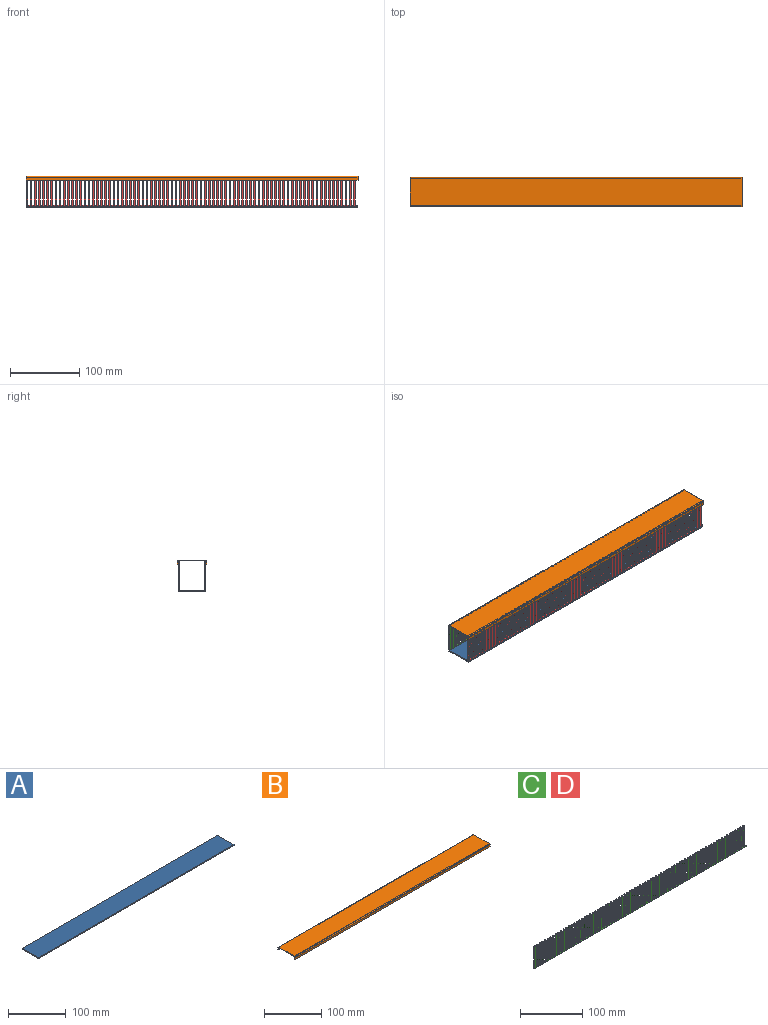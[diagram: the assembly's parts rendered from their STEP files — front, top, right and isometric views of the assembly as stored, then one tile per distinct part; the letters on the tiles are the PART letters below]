
ASSEMBLY  parts=4 mates=3
PART A: 6 faces, bbox 480x40x2 mm
  f0: plane 480.02x2mm, normal (0,1,0), area 960mm2, adj f1,f3,f4,f5
  f1: plane 40x2mm, normal (-1,0,0), area 80mm2, adj f0,f2,f4,f5
  f2: plane 480.02x2mm, normal (0,-1,0), area 960mm2, adj f1,f3,f4,f5
  f3: plane 40x2mm, normal (1,0,0), area 80mm2, adj f0,f2,f4,f5
  f4: plane 480.02x40mm, normal (0,0,1), area 19200.8mm2, adj f0,f1,f2,f3
  f5: plane 480.02x40mm, normal (0,0,-1), area 19200.8mm2, adj f0,f1,f2,f3
PART B: 12 faces, bbox 480.6x42x6 mm
  f0: plane 480.63x1mm, normal (0,0,-1), area 480.6mm2, adj f2,f3,f4,f7
  f1: plane 480.63x1mm, normal (0,0,-1), area 480.6mm2, adj f2,f4,f5,f8
  f2: plane 42x6mm, normal (-1,0,0), area 50.3mm2, adj f0,f1,f3,f5,f6,f7,f8,f9
  f3: plane 480.63x4mm, normal (0,-1,0), area 1922.5mm2, adj f0,f2,f4,f10
  f4: plane 42x6mm, normal (1,0,0), area 50.3mm2, adj f0,f1,f3,f5,f6,f7,f8,f9
  f5: plane 480.63x4mm, normal (0,1,0), area 1922.5mm2, adj f1,f2,f4,f11
  f6: plane 480.63x38mm, normal (0,0,1), area 18264.1mm2, adj f2,f4,f10,f11
  f7: plane 480.63x5mm, normal (0,1,0), area 2403.2mm2, adj f0,f2,f4,f9
  f8: plane 480.63x5mm, normal (0,-1,0), area 2403.2mm2, adj f1,f2,f4,f9
  f9: plane 480.63x40mm, normal (0,0,-1), area 19225.4mm2, adj f2,f4,f7,f8
  f10: cylinder r=2mm len=480.63mm, axis (-1,0,0), area 1510mm2, adj f2,f3,f4,f6
  f11: cylinder r=2mm len=480.63mm, axis (1,0,0), area 1510mm2, adj f2,f4,f5,f6
PART C: 324 faces, bbox 480x2x43.3 mm
  f0: plane 40x2mm, normal (-1,0,0), area 80mm2, adj f3,f5,f6,f8
  f1: plane 3.4x2mm, normal (0,0,1), area 6.8mm2, adj f2,f5,f6,f254
  f2: plane 40x2mm, normal (1,0,0), area 80mm2, adj f1,f3,f5,f6
  f3: cylinder r=1.3mm len=2.6mm, axis (0,1,0), area 8.2mm2, adj f0,f2,f5,f6
  f4: plane 480x2mm, normal (0,0,-1), area 960mm2, adj f5,f6,f214,f319
  f5: plane 480x43.3mm, normal (0,-1,0), area 9483.6mm2, adj f0,f1,f2,f3,f4,f7,f8,f9
  f6: plane 480x43.3mm, normal (0,1,0), area 9483.6mm2, adj f0,f1,f2,f3,f4,f7,f8,f9
  f7: plane 40x2mm, normal (-1,0,0), area 80mm2, adj f5,f6,f10,f12
  f8: plane 3.4x2mm, normal (0,0,1), area 6.8mm2, adj f0,f5,f6,f9
  f9: plane 40x2mm, normal (1,0,0), area 80mm2, adj f5,f6,f8,f10
  f10: cylinder r=1.3mm len=2.6mm, axis (0,1,0), area 8.2mm2, adj f5,f6,f7,f9
  f11: plane 40x2mm, normal (-1,0,0), area 80mm2, adj f5,f6,f14,f16
  f12: plane 3.4x2mm, normal (0,0,1), area 6.8mm2, adj f5,f6,f7,f13
  f13: plane 40x2mm, normal (1,0,0), area 80mm2, adj f5,f6,f12,f14
  f14: cylinder r=1.3mm len=2.6mm, axis (0,1,0), area 8.2mm2, adj f5,f6,f11,f13
  f15: plane 40x2mm, normal (-1,0,0), area 80mm2, adj f5,f6,f18,f20
  f16: plane 3.4x2mm, normal (0,0,1), area 6.8mm2, adj f5,f6,f11,f17
  f17: plane 40x2mm, normal (1,0,0), area 80mm2, adj f5,f6,f16,f18
  f18: cylinder r=1.3mm len=2.6mm, axis (0,1,0), area 8.2mm2, adj f5,f6,f15,f17
  f19: plane 40x2mm, normal (-1,0,0), area 80mm2, adj f5,f6,f22,f24
  f20: plane 3.4x2mm, normal (0,0,1), area 6.8mm2, adj f5,f6,f15,f21
  f21: plane 40x2mm, normal (1,0,0), area 80mm2, adj f5,f6,f20,f22
  f22: cylinder r=1.3mm len=2.6mm, axis (0,1,0), area 8.2mm2, adj f5,f6,f19,f21
  f23: plane 40x2mm, normal (-1,0,0), area 80mm2, adj f5,f6,f26,f28
  f24: plane 3.4x2mm, normal (0,0,1), area 6.8mm2, adj f5,f6,f19,f25
  f25: plane 40x2mm, normal (1,0,0), area 80mm2, adj f5,f6,f24,f26
  f26: cylinder r=1.3mm len=2.6mm, axis (0,1,0), area 8.2mm2, adj f5,f6,f23,f25
  f27: plane 40x2mm, normal (-1,0,0), area 80mm2, adj f5,f6,f30,f32
  f28: plane 3.4x2mm, normal (0,0,1), area 6.8mm2, adj f5,f6,f23,f29
  f29: plane 40x2mm, normal (1,0,0), area 80mm2, adj f5,f6,f28,f30
  f30: cylinder r=1.3mm len=2.6mm, axis (0,1,0), area 8.2mm2, adj f5,f6,f27,f29
  f31: plane 40x2mm, normal (-1,0,0), area 80mm2, adj f5,f6,f34,f36
  f32: plane 3.4x2mm, normal (0,0,1), area 6.8mm2, adj f5,f6,f27,f33
  f33: plane 40x2mm, normal (1,0,0), area 80mm2, adj f5,f6,f32,f34
  f34: cylinder r=1.3mm len=2.6mm, axis (0,1,0), area 8.2mm2, adj f5,f6,f31,f33
  f35: plane 40x2mm, normal (-1,0,0), area 80mm2, adj f5,f6,f38,f40
  f36: plane 3.4x2mm, normal (0,0,1), area 6.8mm2, adj f5,f6,f31,f37
  f37: plane 40x2mm, normal (1,0,0), area 80mm2, adj f5,f6,f36,f38
  f38: cylinder r=1.3mm len=2.6mm, axis (0,1,0), area 8.2mm2, adj f5,f6,f35,f37
  f39: plane 40x2mm, normal (-1,0,0), area 80mm2, adj f5,f6,f42,f44
  f40: plane 3.4x2mm, normal (0,0,1), area 6.8mm2, adj f5,f6,f35,f41
  f41: plane 40x2mm, normal (1,0,0), area 80mm2, adj f5,f6,f40,f42
  f42: cylinder r=1.3mm len=2.6mm, axis (0,1,0), area 8.2mm2, adj f5,f6,f39,f41
  f43: plane 40x2mm, normal (-1,0,0), area 80mm2, adj f5,f6,f46,f48
  f44: plane 3.4x2mm, normal (0,0,1), area 6.8mm2, adj f5,f6,f39,f45
  f45: plane 40x2mm, normal (1,0,0), area 80mm2, adj f5,f6,f44,f46
  f46: cylinder r=1.3mm len=2.6mm, axis (0,1,0), area 8.2mm2, adj f5,f6,f43,f45
  f47: plane 40x2mm, normal (-1,0,0), area 80mm2, adj f5,f6,f50,f52
  f48: plane 3.4x2mm, normal (0,0,1), area 6.8mm2, adj f5,f6,f43,f49
  f49: plane 40x2mm, normal (1,0,0), area 80mm2, adj f5,f6,f48,f50
  f50: cylinder r=1.3mm len=2.6mm, axis (0,1,0), area 8.2mm2, adj f5,f6,f47,f49
  f51: plane 40x2mm, normal (-1,0,0), area 80mm2, adj f5,f6,f54,f56
  f52: plane 3.4x2mm, normal (0,0,1), area 6.8mm2, adj f5,f6,f47,f53
  f53: plane 40x2mm, normal (1,0,0), area 80mm2, adj f5,f6,f52,f54
  f54: cylinder r=1.3mm len=2.6mm, axis (0,1,0), area 8.2mm2, adj f5,f6,f51,f53
  f55: plane 40x2mm, normal (-1,0,0), area 80mm2, adj f5,f6,f58,f60
  f56: plane 3.4x2mm, normal (0,0,1), area 6.8mm2, adj f5,f6,f51,f57
  f57: plane 40x2mm, normal (1,0,0), area 80mm2, adj f5,f6,f56,f58
  f58: cylinder r=1.3mm len=2.6mm, axis (0,1,0), area 8.2mm2, adj f5,f6,f55,f57
  f59: plane 40x2mm, normal (-1,0,0), area 80mm2, adj f5,f6,f62,f64
  f60: plane 3.4x2mm, normal (0,0,1), area 6.8mm2, adj f5,f6,f55,f61
  f61: plane 40x2mm, normal (1,0,0), area 80mm2, adj f5,f6,f60,f62
  f62: cylinder r=1.3mm len=2.6mm, axis (0,1,0), area 8.2mm2, adj f5,f6,f59,f61
  f63: plane 40x2mm, normal (-1,0,0), area 80mm2, adj f5,f6,f66,f68
  f64: plane 3.4x2mm, normal (0,0,1), area 6.8mm2, adj f5,f6,f59,f65
  f65: plane 40x2mm, normal (1,0,0), area 80mm2, adj f5,f6,f64,f66
  f66: cylinder r=1.3mm len=2.6mm, axis (0,1,0), area 8.2mm2, adj f5,f6,f63,f65
  f67: plane 40x2mm, normal (-1,0,0), area 80mm2, adj f5,f6,f70,f72
  f68: plane 3.4x2mm, normal (0,0,1), area 6.8mm2, adj f5,f6,f63,f69
  f69: plane 40x2mm, normal (1,0,0), area 80mm2, adj f5,f6,f68,f70
  f70: cylinder r=1.3mm len=2.6mm, axis (0,1,0), area 8.2mm2, adj f5,f6,f67,f69
  f71: plane 40x2mm, normal (-1,0,0), area 80mm2, adj f5,f6,f74,f76
  f72: plane 3.4x2mm, normal (0,0,1), area 6.8mm2, adj f5,f6,f67,f73
  f73: plane 40x2mm, normal (1,0,0), area 80mm2, adj f5,f6,f72,f74
  f74: cylinder r=1.3mm len=2.6mm, axis (0,1,0), area 8.2mm2, adj f5,f6,f71,f73
  f75: plane 40x2mm, normal (-1,0,0), area 80mm2, adj f5,f6,f78,f80
  f76: plane 3.4x2mm, normal (0,0,1), area 6.8mm2, adj f5,f6,f71,f77
  f77: plane 40x2mm, normal (1,0,0), area 80mm2, adj f5,f6,f76,f78
  f78: cylinder r=1.3mm len=2.6mm, axis (0,1,0), area 8.2mm2, adj f5,f6,f75,f77
  f79: plane 40x2mm, normal (-1,0,0), area 80mm2, adj f5,f6,f82,f84
  f80: plane 3.4x2mm, normal (0,0,1), area 6.8mm2, adj f5,f6,f75,f81
  f81: plane 40x2mm, normal (1,0,0), area 80mm2, adj f5,f6,f80,f82
  f82: cylinder r=1.3mm len=2.6mm, axis (0,1,0), area 8.2mm2, adj f5,f6,f79,f81
  f83: plane 40x2mm, normal (-1,0,0), area 80mm2, adj f5,f6,f86,f88
  f84: plane 3.4x2mm, normal (0,0,1), area 6.8mm2, adj f5,f6,f79,f85
  f85: plane 40x2mm, normal (1,0,0), area 80mm2, adj f5,f6,f84,f86
  f86: cylinder r=1.3mm len=2.6mm, axis (0,1,0), area 8.2mm2, adj f5,f6,f83,f85
  f87: plane 40x2mm, normal (-1,0,0), area 80mm2, adj f5,f6,f90,f92
  f88: plane 3.4x2mm, normal (0,0,1), area 6.8mm2, adj f5,f6,f83,f89
  f89: plane 40x2mm, normal (1,0,0), area 80mm2, adj f5,f6,f88,f90
  f90: cylinder r=1.3mm len=2.6mm, axis (0,1,0), area 8.2mm2, adj f5,f6,f87,f89
  f91: plane 40x2mm, normal (-1,0,0), area 80mm2, adj f5,f6,f94,f96
  f92: plane 3.4x2mm, normal (0,0,1), area 6.8mm2, adj f5,f6,f87,f93
  f93: plane 40x2mm, normal (1,0,0), area 80mm2, adj f5,f6,f92,f94
  f94: cylinder r=1.3mm len=2.6mm, axis (0,1,0), area 8.2mm2, adj f5,f6,f91,f93
  f95: plane 40x2mm, normal (-1,0,0), area 80mm2, adj f5,f6,f98,f100
  f96: plane 3.4x2mm, normal (0,0,1), area 6.8mm2, adj f5,f6,f91,f97
  f97: plane 40x2mm, normal (1,0,0), area 80mm2, adj f5,f6,f96,f98
  f98: cylinder r=1.3mm len=2.6mm, axis (0,1,0), area 8.2mm2, adj f5,f6,f95,f97
  f99: plane 40x2mm, normal (-1,0,0), area 80mm2, adj f5,f6,f102,f104
  f100: plane 3.4x2mm, normal (0,0,1), area 6.8mm2, adj f5,f6,f95,f101
  f101: plane 40x2mm, normal (1,0,0), area 80mm2, adj f5,f6,f100,f102
  f102: cylinder r=1.3mm len=2.6mm, axis (0,1,0), area 8.2mm2, adj f5,f6,f99,f101
  f103: plane 40x2mm, normal (-1,0,0), area 80mm2, adj f5,f6,f106,f108
  f104: plane 3.4x2mm, normal (0,0,1), area 6.8mm2, adj f5,f6,f99,f105
  f105: plane 40x2mm, normal (1,0,0), area 80mm2, adj f5,f6,f104,f106
  f106: cylinder r=1.3mm len=2.6mm, axis (0,1,0), area 8.2mm2, adj f5,f6,f103,f105
  f107: plane 40x2mm, normal (-1,0,0), area 80mm2, adj f5,f6,f110,f112
  f108: plane 3.4x2mm, normal (0,0,1), area 6.8mm2, adj f5,f6,f103,f109
  f109: plane 40x2mm, normal (1,0,0), area 80mm2, adj f5,f6,f108,f110
  f110: cylinder r=1.3mm len=2.6mm, axis (0,1,0), area 8.2mm2, adj f5,f6,f107,f109
  f111: plane 40x2mm, normal (-1,0,0), area 80mm2, adj f5,f6,f114,f116
  f112: plane 3.4x2mm, normal (0,0,1), area 6.8mm2, adj f5,f6,f107,f113
  f113: plane 40x2mm, normal (1,0,0), area 80mm2, adj f5,f6,f112,f114
  f114: cylinder r=1.3mm len=2.6mm, axis (0,1,0), area 8.2mm2, adj f5,f6,f111,f113
  f115: plane 40x2mm, normal (-1,0,0), area 80mm2, adj f5,f6,f118,f120
  f116: plane 3.4x2mm, normal (0,0,1), area 6.8mm2, adj f5,f6,f111,f117
  f117: plane 40x2mm, normal (1,0,0), area 80mm2, adj f5,f6,f116,f118
  f118: cylinder r=1.3mm len=2.6mm, axis (0,1,0), area 8.2mm2, adj f5,f6,f115,f117
  f119: plane 40x2mm, normal (-1,0,0), area 80mm2, adj f5,f6,f122,f124
  f120: plane 3.4x2mm, normal (0,0,1), area 6.8mm2, adj f5,f6,f115,f121
  f121: plane 40x2mm, normal (1,0,0), area 80mm2, adj f5,f6,f120,f122
  f122: cylinder r=1.3mm len=2.6mm, axis (0,1,0), area 8.2mm2, adj f5,f6,f119,f121
  f123: plane 40x2mm, normal (-1,0,0), area 80mm2, adj f5,f6,f126,f128
  f124: plane 3.4x2mm, normal (0,0,1), area 6.8mm2, adj f5,f6,f119,f125
  f125: plane 40x2mm, normal (1,0,0), area 80mm2, adj f5,f6,f124,f126
  f126: cylinder r=1.3mm len=2.6mm, axis (0,1,0), area 8.2mm2, adj f5,f6,f123,f125
  f127: plane 40x2mm, normal (-1,0,0), area 80mm2, adj f5,f6,f130,f132
  f128: plane 3.4x2mm, normal (0,0,1), area 6.8mm2, adj f5,f6,f123,f129
  f129: plane 40x2mm, normal (1,0,0), area 80mm2, adj f5,f6,f128,f130
  f130: cylinder r=1.3mm len=2.6mm, axis (0,1,0), area 8.2mm2, adj f5,f6,f127,f129
  f131: plane 40x2mm, normal (-1,0,0), area 80mm2, adj f5,f6,f134,f136
  f132: plane 3.4x2mm, normal (0,0,1), area 6.8mm2, adj f5,f6,f127,f133
  f133: plane 40x2mm, normal (1,0,0), area 80mm2, adj f5,f6,f132,f134
  f134: cylinder r=1.3mm len=2.6mm, axis (0,1,0), area 8.2mm2, adj f5,f6,f131,f133
  f135: plane 40x2mm, normal (-1,0,0), area 80mm2, adj f5,f6,f138,f140
  f136: plane 3.4x2mm, normal (0,0,1), area 6.8mm2, adj f5,f6,f131,f137
  f137: plane 40x2mm, normal (1,0,0), area 80mm2, adj f5,f6,f136,f138
  f138: cylinder r=1.3mm len=2.6mm, axis (0,1,0), area 8.2mm2, adj f5,f6,f135,f137
  f139: plane 40x2mm, normal (-1,0,0), area 80mm2, adj f5,f6,f142,f144
  f140: plane 3.4x2mm, normal (0,0,1), area 6.8mm2, adj f5,f6,f135,f141
  f141: plane 40x2mm, normal (1,0,0), area 80mm2, adj f5,f6,f140,f142
  f142: cylinder r=1.3mm len=2.6mm, axis (0,1,0), area 8.2mm2, adj f5,f6,f139,f141
  f143: plane 40x2mm, normal (-1,0,0), area 80mm2, adj f5,f6,f146,f148
  f144: plane 3.4x2mm, normal (0,0,1), area 6.8mm2, adj f5,f6,f139,f145
  f145: plane 40x2mm, normal (1,0,0), area 80mm2, adj f5,f6,f144,f146
  f146: cylinder r=1.3mm len=2.6mm, axis (0,1,0), area 8.2mm2, adj f5,f6,f143,f145
  f147: plane 40x2mm, normal (-1,0,0), area 80mm2, adj f5,f6,f150,f152
  f148: plane 3.4x2mm, normal (0,0,1), area 6.8mm2, adj f5,f6,f143,f149
  f149: plane 40x2mm, normal (1,0,0), area 80mm2, adj f5,f6,f148,f150
  f150: cylinder r=1.3mm len=2.6mm, axis (0,1,0), area 8.2mm2, adj f5,f6,f147,f149
  f151: plane 40x2mm, normal (-1,0,0), area 80mm2, adj f5,f6,f154,f156
  f152: plane 3.4x2mm, normal (0,0,1), area 6.8mm2, adj f5,f6,f147,f153
  f153: plane 40x2mm, normal (1,0,0), area 80mm2, adj f5,f6,f152,f154
  f154: cylinder r=1.3mm len=2.6mm, axis (0,1,0), area 8.2mm2, adj f5,f6,f151,f153
  f155: plane 40x2mm, normal (-1,0,0), area 80mm2, adj f5,f6,f158,f160
  f156: plane 3.4x2mm, normal (0,0,1), area 6.8mm2, adj f5,f6,f151,f157
  f157: plane 40x2mm, normal (1,0,0), area 80mm2, adj f5,f6,f156,f158
  f158: cylinder r=1.3mm len=2.6mm, axis (0,1,0), area 8.2mm2, adj f5,f6,f155,f157
  f159: plane 40x2mm, normal (-1,0,0), area 80mm2, adj f5,f6,f162,f164
  f160: plane 3.4x2mm, normal (0,0,1), area 6.8mm2, adj f5,f6,f155,f161
  f161: plane 40x2mm, normal (1,0,0), area 80mm2, adj f5,f6,f160,f162
  f162: cylinder r=1.3mm len=2.6mm, axis (0,1,0), area 8.2mm2, adj f5,f6,f159,f161
  f163: plane 40x2mm, normal (-1,0,0), area 80mm2, adj f5,f6,f166,f168
  f164: plane 3.4x2mm, normal (0,0,1), area 6.8mm2, adj f5,f6,f159,f165
  f165: plane 40x2mm, normal (1,0,0), area 80mm2, adj f5,f6,f164,f166
  f166: cylinder r=1.3mm len=2.6mm, axis (0,1,0), area 8.2mm2, adj f5,f6,f163,f165
  f167: plane 40x2mm, normal (-1,0,0), area 80mm2, adj f5,f6,f170,f172
  f168: plane 3.4x2mm, normal (0,0,1), area 6.8mm2, adj f5,f6,f163,f169
  f169: plane 40x2mm, normal (1,0,0), area 80mm2, adj f5,f6,f168,f170
  f170: cylinder r=1.3mm len=2.6mm, axis (0,1,0), area 8.2mm2, adj f5,f6,f167,f169
  f171: plane 40x2mm, normal (-1,0,0), area 80mm2, adj f5,f6,f174,f176
  f172: plane 3.4x2mm, normal (0,0,1), area 6.8mm2, adj f5,f6,f167,f173
  f173: plane 40x2mm, normal (1,0,0), area 80mm2, adj f5,f6,f172,f174
  f174: cylinder r=1.3mm len=2.6mm, axis (0,1,0), area 8.2mm2, adj f5,f6,f171,f173
  f175: plane 40x2mm, normal (-1,0,0), area 80mm2, adj f5,f6,f178,f180
  f176: plane 3.4x2mm, normal (0,0,1), area 6.8mm2, adj f5,f6,f171,f177
  f177: plane 40x2mm, normal (1,0,0), area 80mm2, adj f5,f6,f176,f178
  f178: cylinder r=1.3mm len=2.6mm, axis (0,1,0), area 8.2mm2, adj f5,f6,f175,f177
  f179: plane 40x2mm, normal (-1,0,0), area 80mm2, adj f5,f6,f182,f184
  f180: plane 3.4x2mm, normal (0,0,1), area 6.8mm2, adj f5,f6,f175,f181
  f181: plane 40x2mm, normal (1,0,0), area 80mm2, adj f5,f6,f180,f182
  f182: cylinder r=1.3mm len=2.6mm, axis (0,1,0), area 8.2mm2, adj f5,f6,f179,f181
  f183: plane 40x2mm, normal (-1,0,0), area 80mm2, adj f5,f6,f186,f188
  f184: plane 3.4x2mm, normal (0,0,1), area 6.8mm2, adj f5,f6,f179,f185
  f185: plane 40x2mm, normal (1,0,0), area 80mm2, adj f5,f6,f184,f186
  f186: cylinder r=1.3mm len=2.6mm, axis (0,1,0), area 8.2mm2, adj f5,f6,f183,f185
  f187: plane 40x2mm, normal (-1,0,0), area 80mm2, adj f5,f6,f190,f192
  f188: plane 3.4x2mm, normal (0,0,1), area 6.8mm2, adj f5,f6,f183,f189
  f189: plane 40x2mm, normal (1,0,0), area 80mm2, adj f5,f6,f188,f190
  f190: cylinder r=1.3mm len=2.6mm, axis (0,1,0), area 8.2mm2, adj f5,f6,f187,f189
  f191: plane 40x2mm, normal (-1,0,0), area 80mm2, adj f5,f6,f194,f196
  f192: plane 3.4x2mm, normal (0,0,1), area 6.8mm2, adj f5,f6,f187,f193
  f193: plane 40x2mm, normal (1,0,0), area 80mm2, adj f5,f6,f192,f194
  f194: cylinder r=1.3mm len=2.6mm, axis (0,1,0), area 8.2mm2, adj f5,f6,f191,f193
  f195: plane 40x2mm, normal (-1,0,0), area 80mm2, adj f5,f6,f198,f200
  f196: plane 3.4x2mm, normal (0,0,1), area 6.8mm2, adj f5,f6,f191,f197
  f197: plane 40x2mm, normal (1,0,0), area 80mm2, adj f5,f6,f196,f198
  f198: cylinder r=1.3mm len=2.6mm, axis (0,1,0), area 8.2mm2, adj f5,f6,f195,f197
  f199: plane 40x2mm, normal (-1,0,0), area 80mm2, adj f5,f6,f202,f243
  f200: plane 3.4x2mm, normal (0,0,1), area 6.8mm2, adj f5,f6,f195,f201
  f201: plane 40x2mm, normal (1,0,0), area 80mm2, adj f5,f6,f200,f202
  f202: cylinder r=1.3mm len=2.6mm, axis (0,1,0), area 8.2mm2, adj f5,f6,f199,f201
  f203: plane 40x2mm, normal (-1,0,0), area 80mm2, adj f5,f6,f206,f208
  f204: plane 3.4x2mm, normal (0,0,1), area 6.8mm2, adj f5,f6,f205,f242
  f205: plane 40x2mm, normal (1,0,0), area 80mm2, adj f5,f6,f204,f206
  f206: cylinder r=1.3mm len=2.6mm, axis (0,1,0), area 8.2mm2, adj f5,f6,f203,f205
  f207: plane 40x2mm, normal (-1,0,0), area 80mm2, adj f5,f6,f210,f211
  f208: plane 3.4x2mm, normal (0,0,1), area 6.8mm2, adj f5,f6,f203,f209
  f209: plane 40x2mm, normal (1,0,0), area 80mm2, adj f5,f6,f208,f210
  f210: cylinder r=1.3mm len=2.6mm, axis (0,1,0), area 8.2mm2, adj f5,f6,f207,f209
  f211: plane 3.4x2mm, normal (0,0,1), area 6.8mm2, adj f5,f6,f207,f212
  f212: plane 40x2mm, normal (1,0,0), area 80mm2, adj f5,f6,f211,f213
  f213: cylinder r=1.3mm len=2.6mm, axis (0,1,0), area 8.2mm2, adj f5,f6,f212,f214
  f214: plane 42x2mm, normal (-1,0,0), area 84mm2, adj f4,f5,f6,f213
  f215: plane 40x2mm, normal (-1,0,0), area 80mm2, adj f5,f6,f218,f231
  f216: plane 3.4x2mm, normal (0,0,1), area 6.8mm2, adj f5,f6,f217,f246
  f217: plane 40x2mm, normal (1,0,0), area 80mm2, adj f5,f6,f216,f218
  f218: cylinder r=1.3mm len=2.6mm, axis (0,1,0), area 8.2mm2, adj f5,f6,f215,f217
  f219: plane 40x2mm, normal (-1,0,0), area 80mm2, adj f5,f6,f222,f239
  f220: plane 3.4x2mm, normal (0,0,1), area 6.8mm2, adj f5,f6,f221,f238
  f221: plane 40x2mm, normal (1,0,0), area 80mm2, adj f5,f6,f220,f222
  f222: cylinder r=1.3mm len=2.6mm, axis (0,1,0), area 8.2mm2, adj f5,f6,f219,f221
  f223: plane 40x2mm, normal (-1,0,0), area 80mm2, adj f5,f6,f226,f235
  f224: plane 3.4x2mm, normal (0,0,1), area 6.8mm2, adj f5,f6,f225,f230
  f225: plane 40x2mm, normal (1,0,0), area 80mm2, adj f5,f6,f224,f226
  f226: cylinder r=1.3mm len=2.6mm, axis (0,1,0), area 8.2mm2, adj f5,f6,f223,f225
  f227: plane 3.4x2mm, normal (0,0,1), area 6.8mm2, adj f5,f6,f228,f234
  f228: plane 40x2mm, normal (1,0,0), area 80mm2, adj f5,f6,f227,f229
  f229: cylinder r=1.3mm len=2.6mm, axis (0,1,0), area 8.2mm2, adj f5,f6,f228,f230
  f230: plane 40x2mm, normal (-1,0,0), area 80mm2, adj f5,f6,f224,f229
  f231: plane 3.4x2mm, normal (0,0,1), area 6.8mm2, adj f5,f6,f215,f232
  f232: plane 40x2mm, normal (1,0,0), area 80mm2, adj f5,f6,f231,f233
  f233: cylinder r=1.3mm len=2.6mm, axis (0,1,0), area 8.2mm2, adj f5,f6,f232,f234
  f234: plane 40x2mm, normal (-1,0,0), area 80mm2, adj f5,f6,f227,f233
  f235: plane 3.4x2mm, normal (0,0,1), area 6.8mm2, adj f5,f6,f223,f236
  f236: plane 40x2mm, normal (1,0,0), area 80mm2, adj f5,f6,f235,f237
  f237: cylinder r=1.3mm len=2.6mm, axis (0,1,0), area 8.2mm2, adj f5,f6,f236,f238
  f238: plane 40x2mm, normal (-1,0,0), area 80mm2, adj f5,f6,f220,f237
  f239: plane 3.4x2mm, normal (0,0,1), area 6.8mm2, adj f5,f6,f219,f240
  f240: plane 40x2mm, normal (1,0,0), area 80mm2, adj f5,f6,f239,f241
  f241: cylinder r=1.3mm len=2.6mm, axis (0,1,0), area 8.2mm2, adj f5,f6,f240,f242
  f242: plane 40x2mm, normal (-1,0,0), area 80mm2, adj f5,f6,f204,f241
  f243: plane 3.4x2mm, normal (0,0,1), area 6.8mm2, adj f5,f6,f199,f244
  f244: plane 40x2mm, normal (1,0,0), area 80mm2, adj f5,f6,f243,f245
  f245: cylinder r=1.3mm len=2.6mm, axis (0,1,0), area 8.2mm2, adj f5,f6,f244,f246
  f246: plane 40x2mm, normal (-1,0,0), area 80mm2, adj f5,f6,f216,f245
  f247: plane 40x2mm, normal (-1,0,0), area 80mm2, adj f5,f6,f250,f251
  f248: plane 3.4x2mm, normal (0,0,1), area 6.8mm2, adj f5,f6,f249,f262
  f249: plane 40x2mm, normal (1,0,0), area 80mm2, adj f5,f6,f248,f250
  f250: cylinder r=1.3mm len=2.6mm, axis (0,1,0), area 8.2mm2, adj f5,f6,f247,f249
  f251: plane 3.4x2mm, normal (0,0,1), area 6.8mm2, adj f5,f6,f247,f252
  f252: plane 40x2mm, normal (1,0,0), area 80mm2, adj f5,f6,f251,f253
  f253: cylinder r=1.3mm len=2.6mm, axis (0,1,0), area 8.2mm2, adj f5,f6,f252,f254
  f254: plane 40x2mm, normal (-1,0,0), area 80mm2, adj f1,f5,f6,f253
  f255: plane 40x2mm, normal (-1,0,0), area 80mm2, adj f5,f6,f258,f259
  f256: plane 3.4x2mm, normal (0,0,1), area 6.8mm2, adj f5,f6,f257,f270
  f257: plane 40x2mm, normal (1,0,0), area 80mm2, adj f5,f6,f256,f258
  f258: cylinder r=1.3mm len=2.6mm, axis (0,1,0), area 8.2mm2, adj f5,f6,f255,f257
  f259: plane 3.4x2mm, normal (0,0,1), area 6.8mm2, adj f5,f6,f255,f260
  f260: plane 40x2mm, normal (1,0,0), area 80mm2, adj f5,f6,f259,f261
  f261: cylinder r=1.3mm len=2.6mm, axis (0,1,0), area 8.2mm2, adj f5,f6,f260,f262
  f262: plane 40x2mm, normal (-1,0,0), area 80mm2, adj f5,f6,f248,f261
  f263: plane 40x2mm, normal (-1,0,0), area 80mm2, adj f5,f6,f266,f267
  f264: plane 3.4x2mm, normal (0,0,1), area 6.8mm2, adj f5,f6,f265,f278
  f265: plane 40x2mm, normal (1,0,0), area 80mm2, adj f5,f6,f264,f266
  f266: cylinder r=1.3mm len=2.6mm, axis (0,1,0), area 8.2mm2, adj f5,f6,f263,f265
  f267: plane 3.4x2mm, normal (0,0,1), area 6.8mm2, adj f5,f6,f263,f268
  f268: plane 40x2mm, normal (1,0,0), area 80mm2, adj f5,f6,f267,f269
  f269: cylinder r=1.3mm len=2.6mm, axis (0,1,0), area 8.2mm2, adj f5,f6,f268,f270
  f270: plane 40x2mm, normal (-1,0,0), area 80mm2, adj f5,f6,f256,f269
  f271: plane 40x2mm, normal (-1,0,0), area 80mm2, adj f5,f6,f274,f275
  f272: plane 3.4x2mm, normal (0,0,1), area 6.8mm2, adj f5,f6,f273,f286
  f273: plane 40x2mm, normal (1,0,0), area 80mm2, adj f5,f6,f272,f274
  f274: cylinder r=1.3mm len=2.6mm, axis (0,1,0), area 8.2mm2, adj f5,f6,f271,f273
  f275: plane 3.4x2mm, normal (0,0,1), area 6.8mm2, adj f5,f6,f271,f276
  f276: plane 40x2mm, normal (1,0,0), area 80mm2, adj f5,f6,f275,f277
  f277: cylinder r=1.3mm len=2.6mm, axis (0,1,0), area 8.2mm2, adj f5,f6,f276,f278
  f278: plane 40x2mm, normal (-1,0,0), area 80mm2, adj f5,f6,f264,f277
  f279: plane 40x2mm, normal (-1,0,0), area 80mm2, adj f5,f6,f282,f283
  f280: plane 3.4x2mm, normal (0,0,1), area 6.8mm2, adj f5,f6,f281,f294
  f281: plane 40x2mm, normal (1,0,0), area 80mm2, adj f5,f6,f280,f282
  f282: cylinder r=1.3mm len=2.6mm, axis (0,1,0), area 8.2mm2, adj f5,f6,f279,f281
  f283: plane 3.4x2mm, normal (0,0,1), area 6.8mm2, adj f5,f6,f279,f284
  f284: plane 40x2mm, normal (1,0,0), area 80mm2, adj f5,f6,f283,f285
  f285: cylinder r=1.3mm len=2.6mm, axis (0,1,0), area 8.2mm2, adj f5,f6,f284,f286
  f286: plane 40x2mm, normal (-1,0,0), area 80mm2, adj f5,f6,f272,f285
  f287: plane 40x2mm, normal (-1,0,0), area 80mm2, adj f5,f6,f290,f291
  f288: plane 3.4x2mm, normal (0,0,1), area 6.8mm2, adj f5,f6,f289,f302
  f289: plane 40x2mm, normal (1,0,0), area 80mm2, adj f5,f6,f288,f290
  f290: cylinder r=1.3mm len=2.6mm, axis (0,1,0), area 8.2mm2, adj f5,f6,f287,f289
  f291: plane 3.4x2mm, normal (0,0,1), area 6.8mm2, adj f5,f6,f287,f292
  f292: plane 40x2mm, normal (1,0,0), area 80mm2, adj f5,f6,f291,f293
  f293: cylinder r=1.3mm len=2.6mm, axis (0,1,0), area 8.2mm2, adj f5,f6,f292,f294
  f294: plane 40x2mm, normal (-1,0,0), area 80mm2, adj f5,f6,f280,f293
  f295: plane 40x2mm, normal (-1,0,0), area 80mm2, adj f5,f6,f298,f299
  f296: plane 3.4x2mm, normal (0,0,1), area 6.8mm2, adj f5,f6,f297,f310
  f297: plane 40x2mm, normal (1,0,0), area 80mm2, adj f5,f6,f296,f298
  f298: cylinder r=1.3mm len=2.6mm, axis (0,1,0), area 8.2mm2, adj f5,f6,f295,f297
  f299: plane 3.4x2mm, normal (0,0,1), area 6.8mm2, adj f5,f6,f295,f300
  f300: plane 40x2mm, normal (1,0,0), area 80mm2, adj f5,f6,f299,f301
  f301: cylinder r=1.3mm len=2.6mm, axis (0,1,0), area 8.2mm2, adj f5,f6,f300,f302
  f302: plane 40x2mm, normal (-1,0,0), area 80mm2, adj f5,f6,f288,f301
  f303: plane 40x2mm, normal (-1,0,0), area 80mm2, adj f5,f6,f306,f307
  f304: plane 3.4x2mm, normal (0,0,1), area 6.8mm2, adj f5,f6,f305,f318
  f305: plane 40x2mm, normal (1,0,0), area 80mm2, adj f5,f6,f304,f306
  f306: cylinder r=1.3mm len=2.6mm, axis (0,1,0), area 8.2mm2, adj f5,f6,f303,f305
  f307: plane 3.4x2mm, normal (0,0,1), area 6.8mm2, adj f5,f6,f303,f308
  f308: plane 40x2mm, normal (1,0,0), area 80mm2, adj f5,f6,f307,f309
  f309: cylinder r=1.3mm len=2.6mm, axis (0,1,0), area 8.2mm2, adj f5,f6,f308,f310
  f310: plane 40x2mm, normal (-1,0,0), area 80mm2, adj f5,f6,f296,f309
  f311: plane 40x2mm, normal (-1,0,0), area 80mm2, adj f5,f6,f314,f315
  f312: plane 3.4x2mm, normal (0,0,1), area 6.8mm2, adj f5,f6,f313,f323
  f313: plane 40x2mm, normal (1,0,0), area 80mm2, adj f5,f6,f312,f314
  f314: cylinder r=1.3mm len=2.6mm, axis (0,1,0), area 8.2mm2, adj f5,f6,f311,f313
  f315: plane 3.4x2mm, normal (0,0,1), area 6.8mm2, adj f5,f6,f311,f316
  f316: plane 40x2mm, normal (1,0,0), area 80mm2, adj f5,f6,f315,f317
  f317: cylinder r=1.3mm len=2.6mm, axis (0,1,0), area 8.2mm2, adj f5,f6,f316,f318
  f318: plane 40x2mm, normal (-1,0,0), area 80mm2, adj f5,f6,f304,f317
  f319: plane 2x2mm, normal (1,0,0), area 4mm2, adj f4,f5,f6,f320
  f320: plane 3.4x2mm, normal (0,0,1), area 6.8mm2, adj f5,f6,f319,f321
  f321: plane 40x2mm, normal (1,0,0), area 80mm2, adj f5,f6,f320,f322
  f322: cylinder r=1.3mm len=2.6mm, axis (0,1,0), area 8.2mm2, adj f5,f6,f321,f323
  f323: plane 40x2mm, normal (-1,0,0), area 80mm2, adj f5,f6,f312,f322
PART D: same geometry as C
PLACE A t=(-161.53,-10.42,-113.63)mm
PLACE B t=(-160.6,-59.81,-73.63)mm
PLACE C t=(-161.53,-10.42,-126.22)mm
PLACE D t=(-161.53,-48.42,-126.22)mm
MATE fastened C.f4 <-> A.f4  axis (0,0,-1) through (-211.45,-10.42,-111.63)mm
MATE fastened D.f4 <-> A.f4  axis (0,0,-1) through (-211.45,-50.42,-111.63)mm
MATE slider A.f1 <-> B.f2  axis (-1,0,0) through (-211.45,-30.42,-111.63)mm
